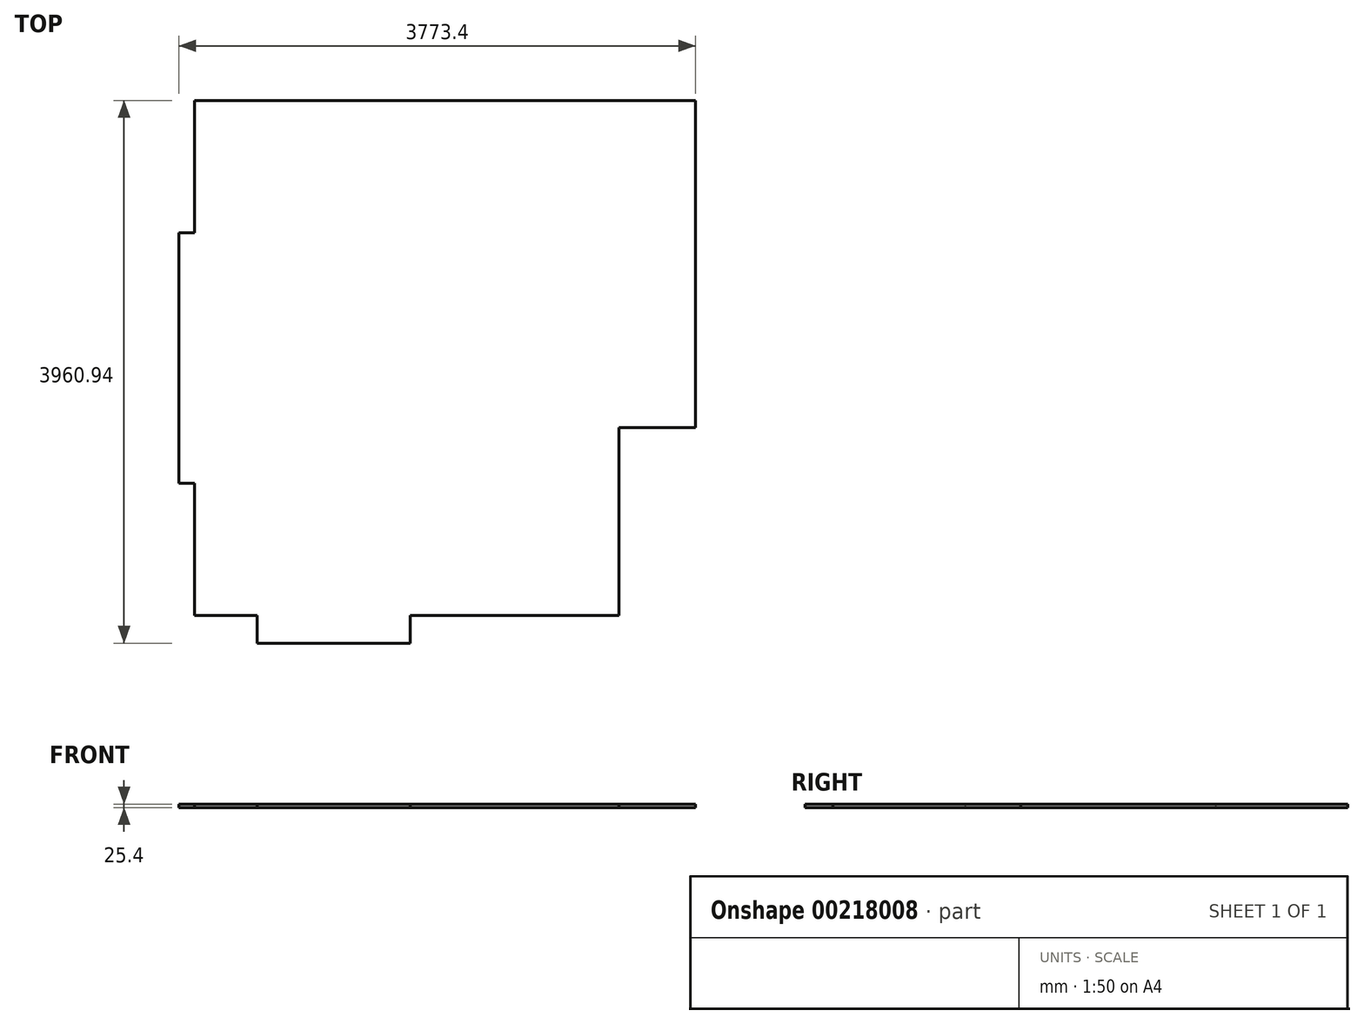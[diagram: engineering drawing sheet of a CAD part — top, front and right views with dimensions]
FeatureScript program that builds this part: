
annotation { "Feature Type Name" : "Feature", "Feature Type Description" : "" }
export const myFeature = defineFeature(function(context is Context, id is Id, definition is map)
    precondition{}
    {
        {
            var Q0;
            Q0=qCreatedBy(makeId("Top.planeOp"),FACE);
            var sketch = newSketch(context, id + "F0", { "sketchPlane" : qUnion([Q0])});
            skLineSegment(sketch, "E0", {"start": v(-1574.8, 2794) * mm, "end": v(-1574.8, 1828.8) * mm});
            skLineSegment(sketch, "E1", {"start": v(-1690.6, 1828.8) * mm, "end": v(-1574.8, 1828.8) * mm});
            skLineSegment(sketch, "E2", {"start": v(-1690.6, 1828.8) * mm, "end": v(-1690.6, 0) * mm});
            skLineSegment(sketch, "E3", {"start": v(-1574.8, 0) * mm, "end": v(-1690.6, 0) * mm});
            skLineSegment(sketch, "E4", {"start": v(-1574.8, 0) * mm, "end": v(-1574.8, -965.2) * mm});
            skLineSegment(sketch, "E5", {"start": v(-1574.8, -965.2) * mm, "end": v(-1117.6, -965.2) * mm});
            skLineSegment(sketch, "E6", {"start": v(-1117.6, -965.2) * mm, "end": v(-1117.6, -1166.94) * mm});
            skLineSegment(sketch, "E7", {"start": v(-1117.6, -1166.94) * mm, "end": v(0, -1166.94) * mm});
            skLineSegment(sketch, "E8", {"start": v(0, -1166.94) * mm, "end": v(0, -965.2) * mm});
            skLineSegment(sketch, "E9", {"start": v(2082.8, -965.2) * mm, "end": v(2082.8, -959.92) * mm});
            skLineSegment(sketch, "E10", {"start": v(-1574.8, 2794) * mm, "end": v(2082.8, 2794) * mm});
            skLineSegment(sketch, "E11", {"start": v(0, -965.2) * mm, "end": v(1524, -965.2) * mm});
            skLineSegment(sketch, "E12", {"start": v(1524, -965.2) * mm, "end": v(1524, 406.4) * mm});
            skLineSegment(sketch, "E13", {"start": v(1524, 406.4) * mm, "end": v(2082.8, 406.4) * mm});
            skLineSegment(sketch, "E14.trimOffspring", {"start": v(2082.8, 406.4) * mm, "end": v(2082.8, 2794) * mm});
            skSolve(sketch);
        }
        {
            var Q0;
            Q0=makeQuery(id+"F0.imprint","IMPRINT",FACE,{"disambiguationData":[TD([[makeQuery(id+"F0.imprint","IMPRINT",EDGE,{"derivedFrom":sQuery(id+"F0.wireOp",EDGE,"E0")}),1.0]])]});
            extrude(context, id + "F1", {"entities" : qUnion([Q0]), "depth" : 25.4 * mm});
        }
    });
